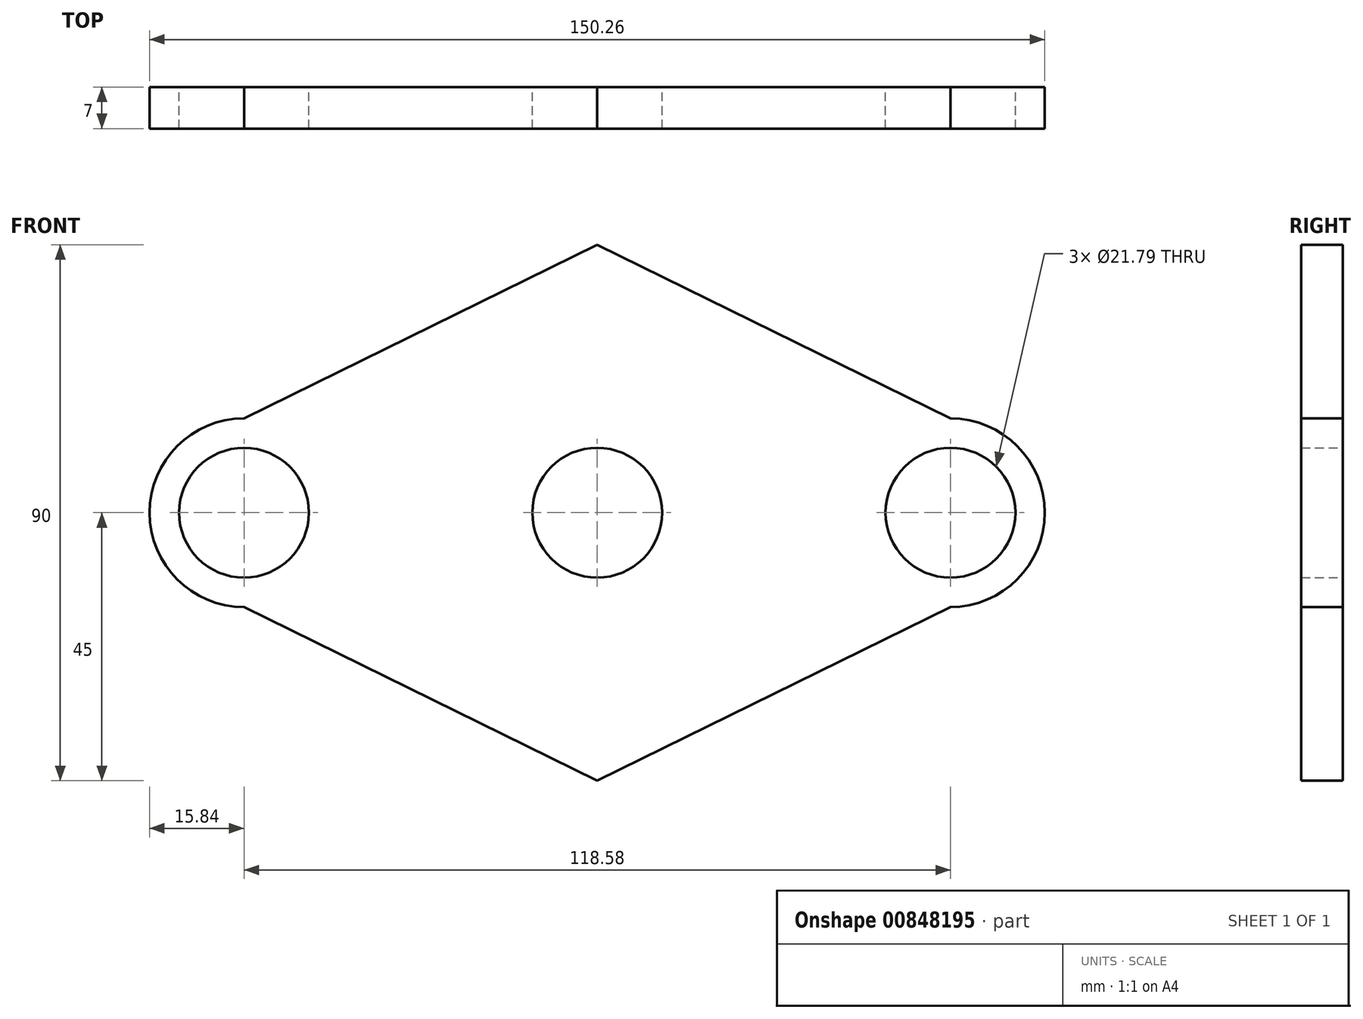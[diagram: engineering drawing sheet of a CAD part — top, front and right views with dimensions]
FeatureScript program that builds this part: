
annotation { "Feature Type Name" : "Feature", "Feature Type Description" : "" }
export const myFeature = defineFeature(function(context is Context, id is Id, definition is map)
    precondition{}
    {
        {
            var Q0;
            Q0=qCreatedBy(makeId("Front.planeOp"),FACE);
            var sketch = newSketch(context, id + "F0", { "sketchPlane" : qUnion([Q0])});
            skCircle(sketch, "E0", {"center": v(0, 0) * mm, "radius": 10.9 * mm});
            skCircle(sketch, "E1", {"center": v(0, 0) * mm, "radius": 15.84 * mm});
            skCircle(sketch, "E2", {"center": v(-59.3, 0) * mm, "radius": 10.9 * mm});
            skCircle(sketch, "E3", {"center": v(-59.3, 0) * mm, "radius": 15.84 * mm});
            skCircle(sketch, "E4", {"center": v(59.3, 0) * mm, "radius": 15.84 * mm});
            skCircle(sketch, "E5", {"center": v(59.3, 0) * mm, "radius": 10.9 * mm});
            skLineSegment(sketch, "E6", {"start": v(-59.3, 15.84) * mm, "end": v(59.3, 15.84) * mm});
            skLineSegment(sketch, "E7", {"start": v(-59.3, -15.84) * mm, "end": v(59.3, -15.84) * mm});
            skLineSegment(sketch, "E8", {"start": v(59.3, 15.84) * mm, "end": v(0, 45) * mm});
            skLineSegment(sketch, "E9", {"start": v(0, 45) * mm, "end": v(-59.3, 15.84) * mm});
            skLineSegment(sketch, "E10", {"start": v(59.3, -15.84) * mm, "end": v(0, -45) * mm});
            skLineSegment(sketch, "E11", {"start": v(0, -45) * mm, "end": v(-59.3, -15.84) * mm});
            skSolve(sketch);
        }
        {
            var Q0;
            Q0=makeQuery(id+"F0.imprint","IMPRINT",FACE,{"disambiguationData":[TD([[makeQuery(id+"F0.imprint","IMPRINT",EDGE,{"derivedFrom":sQuery(id+"F0.wireOp",EDGE,"E2")}),-1.0]])]});
            var Q1;
            {var subQ3=sQuery(id+"F0.wireOp",EDGE,"E10");Q1=makeQuery(id+"F0.imprint","IMPRINT",FACE,{"disambiguationData":[TD([[makeQuery(id+"F0.imprint","IMPRINT",EDGE,{"derivedFrom":subQ3}),-1.0]])]});}
            var Q2;
            {var subQ3=sQuery(id+"F0.wireOp",EDGE,"E8");Q2=makeQuery(id+"F0.imprint","IMPRINT",FACE,{"disambiguationData":[TD([[makeQuery(id+"F0.imprint","IMPRINT",EDGE,{"derivedFrom":subQ3}),1.0]])]});}
            var Q3;
            {var subQ0=sQuery(id+"F0.wireOp",EDGE,"E6");var subQ1=sQuery(id+"F0.wireOp",EDGE,"E1");var subQ2=makeQuery(id+"F0.imprint","INTERSECT",VERTEX,{"derivedFrom":[subQ1,subQ0]});Q3=makeQuery(id+"F0.imprint","IMPRINT",FACE,{"disambiguationData":[TD([[makeQuery(id+"F0.imprint","IMPRINT",EDGE,{"disambiguationData":[TD([[subQ2,-1.0]])],"derivedFrom":subQ1}),-1.0]])]});}
            var Q4;
            {var subQ0=sQuery(id+"F0.wireOp",EDGE,"E6");var subQ1=sQuery(id+"F0.wireOp",EDGE,"E1");var subQ2=makeQuery(id+"F0.imprint","INTERSECT",VERTEX,{"derivedFrom":[subQ1,subQ0]});Q4=makeQuery(id+"F0.imprint","IMPRINT",FACE,{"disambiguationData":[TD([[makeQuery(id+"F0.imprint","IMPRINT",EDGE,{"disambiguationData":[TD([[subQ2,1.0]])],"derivedFrom":subQ1}),-1.0]])]});}
            var Q5;
            Q5=makeQuery(id+"F0.imprint","IMPRINT",FACE,{"disambiguationData":[TD([[makeQuery(id+"F0.imprint","IMPRINT",EDGE,{"derivedFrom":sQuery(id+"F0.wireOp",EDGE,"E5")}),-1.0]])]});
            var Q6;
            Q6=makeQuery(id+"F0.imprint","IMPRINT",FACE,{"disambiguationData":[TD([[makeQuery(id+"F0.imprint","IMPRINT",EDGE,{"derivedFrom":sQuery(id+"F0.wireOp",EDGE,"E0")}),-1.0]])]});
            extrude(context, id + "F1", {"entities" : qUnion([Q0, Q1, Q2, Q3, Q4, Q5, Q6]), "depth" : 7 * mm, "offsetDistance" : 25 * mm});
        }
    });
